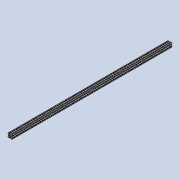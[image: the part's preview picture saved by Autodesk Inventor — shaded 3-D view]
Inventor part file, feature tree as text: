
AUTODESK INVENTOR PART (.ipt)
format: ipt  version: 2022 (Build 260153000, 153)  size: 296,960 bytes
history: native  units: in
note: dims shown in document units (in); Inventor stores cm internally (conversion verified against a paired STEP export)
features: extrude x1, sketch x1, projected_geometry x1, mirror x1
ambient origin geometry x8: Origin, YZ Plane, XZ Plane, XY Plane, X Axis, Y Axis, Z Axis, Center Point
bodies: Solid1 (feature_tree)
feature tree (4):
  extrude  "Extrusion1"  [1 undecoded]
  sketch  "Sketch1"  dims[d0=16.0in d1=0.0in]
  projected_geometry  "Projected Loop1"
  mirror  "Mirror2"
note: 1 required parameter value undecoded (feature->parameter linkage not recoverable at this tier; creation-order binding heuristic only, values carry confidence <= 0.55)
